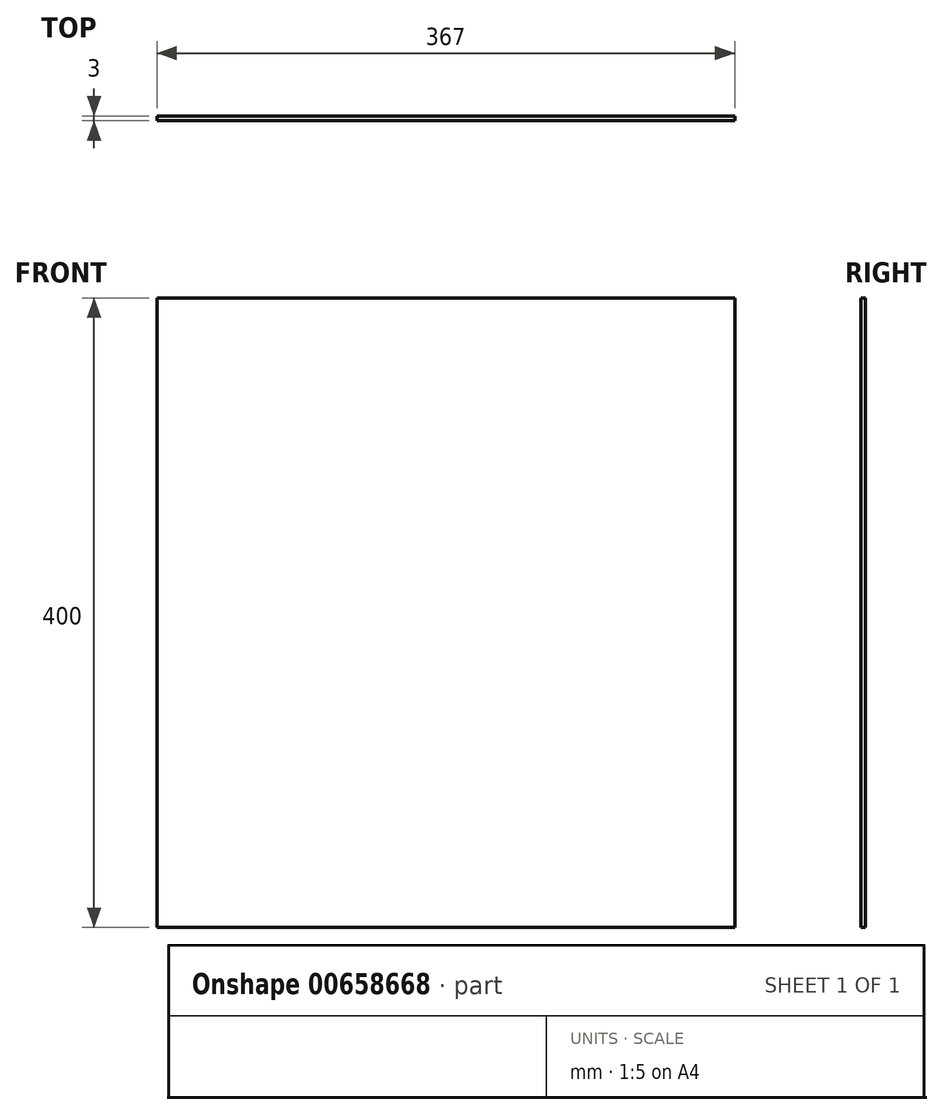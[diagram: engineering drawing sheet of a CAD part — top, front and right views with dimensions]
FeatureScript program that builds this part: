
annotation { "Feature Type Name" : "Feature", "Feature Type Description" : "" }
export const myFeature = defineFeature(function(context is Context, id is Id, definition is map)
    precondition{}
    {
        {
            var Q0;
            Q0=qCreatedBy(makeId("Front.planeOp"),FACE);
            var sketch = newSketch(context, id + "F0", { "sketchPlane" : qUnion([Q0])});
            skLineSegment(sketch, "E0.bottom", {"start": v(183.5, -200) * mm, "end": v(-183.5, -200) * mm});
            skLineSegment(sketch, "E0.top", {"start": v(183.5, 200) * mm, "end": v(-183.5, 200) * mm});
            skLineSegment(sketch, "E0.left", {"start": v(183.5, -200) * mm, "end": v(183.5, 200) * mm});
            skLineSegment(sketch, "E0.right", {"start": v(-183.5, -200) * mm, "end": v(-183.5, 200) * mm});
            skPoint(sketch, "E0.middle", {"position": v(0, 0) * mm});
            skSolve(sketch);
        }
        {
            var Q0;
            Q0=makeQuery(id+"F0.imprint","IMPRINT",FACE,{"disambiguationData":[TD([[makeQuery(id+"F0.imprint","IMPRINT",EDGE,{"derivedFrom":sQuery(id+"F0.wireOp",EDGE,"E0.bottom")}),-1.0]])]});
            extrude(context, id + "F1", {"entities" : qUnion([Q0]), "depth" : 3 * mm, "offsetDistance" : 25 * mm});
        }
    });
